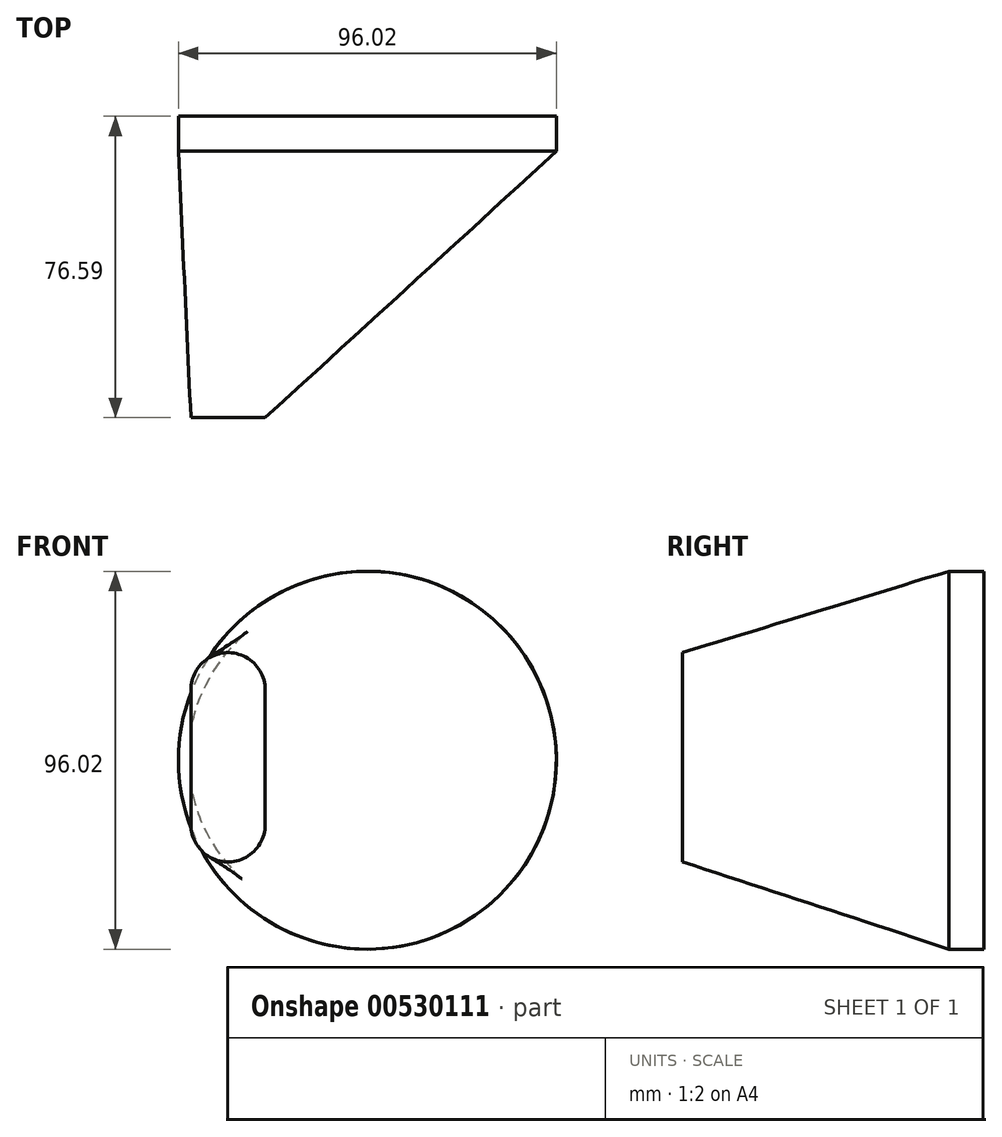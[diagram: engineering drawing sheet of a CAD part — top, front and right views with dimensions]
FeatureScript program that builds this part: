
annotation { "Feature Type Name" : "Feature", "Feature Type Description" : "" }
export const myFeature = defineFeature(function(context is Context, id is Id, definition is map)
    precondition{}
    {
        {
            var Q0;
            Q0=qCreatedBy(makeId("Front.planeOp"),FACE);
            var sketch = newSketch(context, id + "F0", { "sketchPlane" : qUnion([Q0])});
            skCircle(sketch, "E0", {"center": v(0, 0) * mm, "radius": 48.01 * mm});
            skSolve(sketch);
        }
        {
            var Q0;
            Q0=qCreatedBy(makeId("Front.planeOp"),FACE);
            cPlane(context, id + "F1", {"entities" : qUnion([Q0]), "cplaneType" : CPlaneType.OFFSET, "offset" : 72.14 * mm, "width" : 152.4 * mm, "height" : 152.4 * mm});
        }
        {
            var Q0;
            Q0=qCreatedBy(id+"F1.planeOp",FACE);
            var sketch = newSketch(context, id + "F2", { "sketchPlane" : qUnion([Q0])});
            skLineSegment(sketch, "E1.bottom", {"start": v(-44.84, 17.89) * mm, "end": v(-25.95, 17.89) * mm, "construction": true});
            skLineSegment(sketch, "E1.top", {"start": v(-44.84, -16.37) * mm, "end": v(-25.95, -16.37) * mm, "construction": true});
            skLineSegment(sketch, "E1.left", {"start": v(-44.84, 17.89) * mm, "end": v(-44.84, -16.37) * mm});
            skLineSegment(sketch, "E1.right", {"start": v(-25.95, 17.89) * mm, "end": v(-25.95, -16.37) * mm});
            skArc(sketch, "E2", {"start": v(-25.95, 17.89) * mm, "mid": v(-35.4, 27.33) * mm, "end": v(-44.84, 17.89) * mm});
            skArc(sketch, "E3", {"start": v(-44.84, -16.37) * mm, "mid": v(-35.4, -25.82) * mm, "end": v(-25.95, -16.37) * mm});
            skSolve(sketch);
        }
        {
            var Q0;
            Q0=makeQuery(id+"F0.imprint","IMPRINT",FACE,{"disambiguationData":[TD([[makeQuery(id+"F0.imprint","IMPRINT",EDGE,{"derivedFrom":sQuery(id+"F0.wireOp",EDGE,"E0")}),1.0]])]});
            extrude(context, id + "F3", {"entities" : qUnion([Q0]), "endBound" : BoundingType.SYMMETRIC, "depth" : 8.9 * mm, "offsetDistance" : 25.4 * mm});
        }
        {
            var Q0;
            Q0=makeQuery(id+"F3.opExtrude","CAP_FACE",FACE,{"disambiguationData":[OSD([sQuery(id+"F0.wireOp",EDGE,"E0")])],"isStart":false});
            var sketch = newSketch(context, id + "F4", { "sketchPlane" : qUnion([Q0])});
            skArc(sketch, "E4", {"start": v(-20.47, 43.43) * mm, "mid": v(-48, -0.62) * mm, "end": v(-19.33, -43.95) * mm});
            skArc(sketch, "E5", {"start": v(17.72, 44.62) * mm, "mid": v(-1.5, 47.99) * mm, "end": v(-20.47, 43.43) * mm});
            skArc(sketch, "E6", {"start": v(26, -40.36) * mm, "mid": v(47.78, 4.65) * mm, "end": v(17.72, 44.62) * mm});
            skArc(sketch, "E7", {"start": v(-19.33, -43.95) * mm, "mid": v(3.78, -47.86) * mm, "end": v(26, -40.36) * mm});
            skSolve(sketch);
        }
        {
            var Q0;
            Q0=makeQuery(id+"F4.imprint","IMPRINT",FACE,{"disambiguationData":[TD([[makeQuery(id+"F4.imprint","IMPRINT",EDGE,{"derivedFrom":sQuery(id+"F4.wireOp",EDGE,"E4")}),1.0]])]});
            var Q1;
            Q1=makeQuery(id+"F2.imprint","IMPRINT",FACE,{"disambiguationData":[TD([[makeQuery(id+"F2.imprint","IMPRINT",EDGE,{"derivedFrom":sQuery(id+"F2.wireOp",EDGE,"E1.left")}),1.0]])]});
            loft(context, id + "F5", {"sheetProfilesArray" : [{ "sheetProfileEntities" : qUnion([Q0]) }, { "sheetProfileEntities" : qUnion([Q1]) }]});
        }
    });
